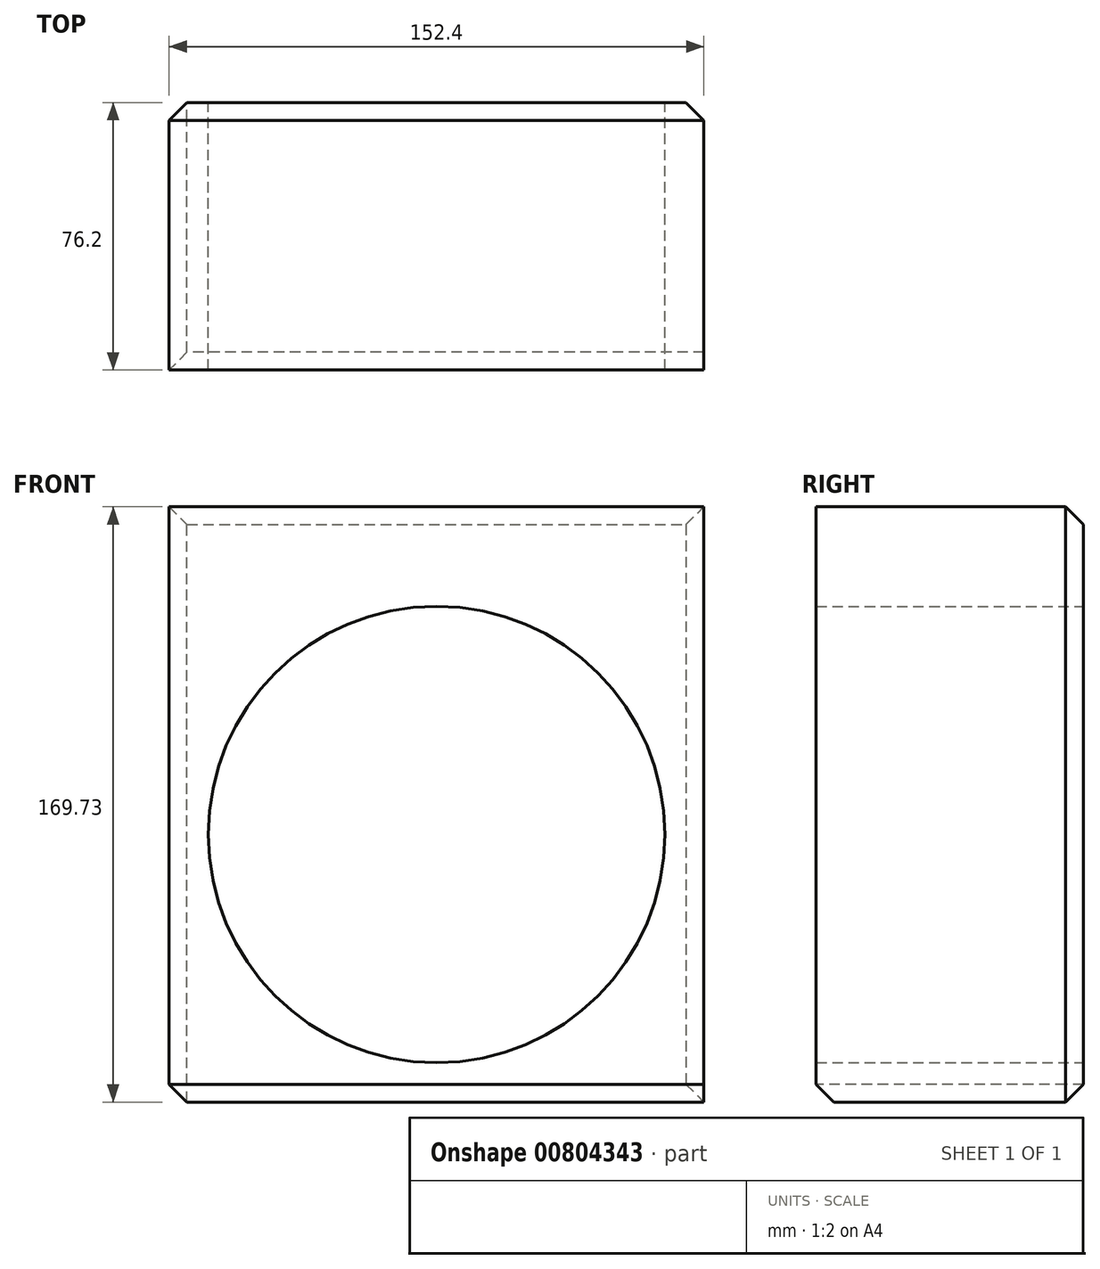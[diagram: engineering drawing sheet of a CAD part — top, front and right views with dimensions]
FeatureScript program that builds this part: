
annotation { "Feature Type Name" : "Feature", "Feature Type Description" : "" }
export const myFeature = defineFeature(function(context is Context, id is Id, definition is map)
    precondition{}
    {
        {
            var Q0;
            Q0=qCreatedBy(makeId("Front.planeOp"),FACE);
            var sketch = newSketch(context, id + "F0", { "sketchPlane" : qUnion([Q0])});
            skLineSegment(sketch, "E0.bottom", {"start": v(-76.2, 93.44) * mm, "end": v(76.2, 93.44) * mm});
            skLineSegment(sketch, "E0.top", {"start": v(-76.2, -76.3) * mm, "end": v(76.2, -76.3) * mm});
            skLineSegment(sketch, "E0.left", {"start": v(-76.2, 93.44) * mm, "end": v(-76.2, -76.3) * mm});
            skLineSegment(sketch, "E0.right", {"start": v(76.2, 93.44) * mm, "end": v(76.2, -76.3) * mm});
            skSolve(sketch);
        }
        {
            var Q0;
            Q0 = qSketchRegion(id + "F0", true);
            extrude(context, id + "F1", {"entities" : qUnion([Q0]), "depth" : 76.2 * mm, "offsetDistance" : 25.4 * mm});
        }
        {
            var Q0;
            Q0=makeQuery(id+"F1.opExtrude","CAP_FACE",FACE,{"disambiguationData":[OSD([sQuery(id+"F0.wireOp",EDGE,"E0.bottom"),sQuery(id+"F0.wireOp",EDGE,"E0.top"),sQuery(id+"F0.wireOp",EDGE,"E0.left"),sQuery(id+"F0.wireOp",EDGE,"E0.right")])],"isStart":true});
            var sketch = newSketch(context, id + "F2", { "sketchPlane" : qUnion([Q0])});
            skCircle(sketch, "E1", {"center": v(0, 0) * mm, "radius": 65.07 * mm});
            skSolve(sketch);
        }
        {
            var Q0;
            Q0 = qSketchRegion(id + "F2", true);
            extrude(context, id + "F3", {"entities" : qUnion([Q0]), "operationType" : NewBodyOperationType.REMOVE, "endBound" : BoundingType.THROUGH_ALL, "oppositeDirection" : true, "depth" : 25.4 * mm, "offsetDistance" : 25.4 * mm});
        }
        {
            var Q0;
            Q0=makeQuery(id+"F1.opExtrude","CAP_EDGE",EDGE,{"disambiguationData":[OSD([sQuery(id+"F0.wireOp",EDGE,"E0.left")])],"isStart":true});
            var Q1;
            Q1=makeQuery(id+"F1.opExtrude","CAP_EDGE",EDGE,{"disambiguationData":[OSD([sQuery(id+"F0.wireOp",EDGE,"E0.bottom")])],"isStart":true});
            var Q2;
            Q2=makeQuery(id+"F1.opExtrude","CAP_EDGE",EDGE,{"disambiguationData":[OSD([sQuery(id+"F0.wireOp",EDGE,"E0.right")])],"isStart":true});
            var Q3;
            Q3=makeQuery(id+"F1.opExtrude","CAP_EDGE",EDGE,{"disambiguationData":[OSD([sQuery(id+"F0.wireOp",EDGE,"E0.top")])],"isStart":true});
            var Q4;
            Q4=makeQuery(id+"F3.boolean.opBoolean","COPY",EDGE,{"derivedFrom":makeQuery(id+"F3.opExtrude","CAP_EDGE",EDGE,{"disambiguationData":[OSD([sQuery(id+"F2.wireOp",EDGE,"E1")])],"isStart":true})});
            var Q5;
            Q5=makeQuery(id+"F1.opExtrude","CAP_EDGE",EDGE,{"disambiguationData":[OSD([sQuery(id+"F0.wireOp",EDGE,"E0.top")])],"isStart":false});
            var Q6;
            Q6=makeQuery(id+"F1.opExtrude","SWEPT_EDGE",EDGE,{"disambiguationData":[OSD([sQuery(id+"F0.wireOp",EDGE,"E0.top"),sQuery(id+"F0.wireOp",EDGE,"E0.left")])]});
            chamfer(context, id + "F4", {"entities" : qUnion([Q0, Q1, Q2, Q3, Q4, Q5, Q6]), "width" : 5.08 * mm, "tangentPropagation" : true});
        }
    });
